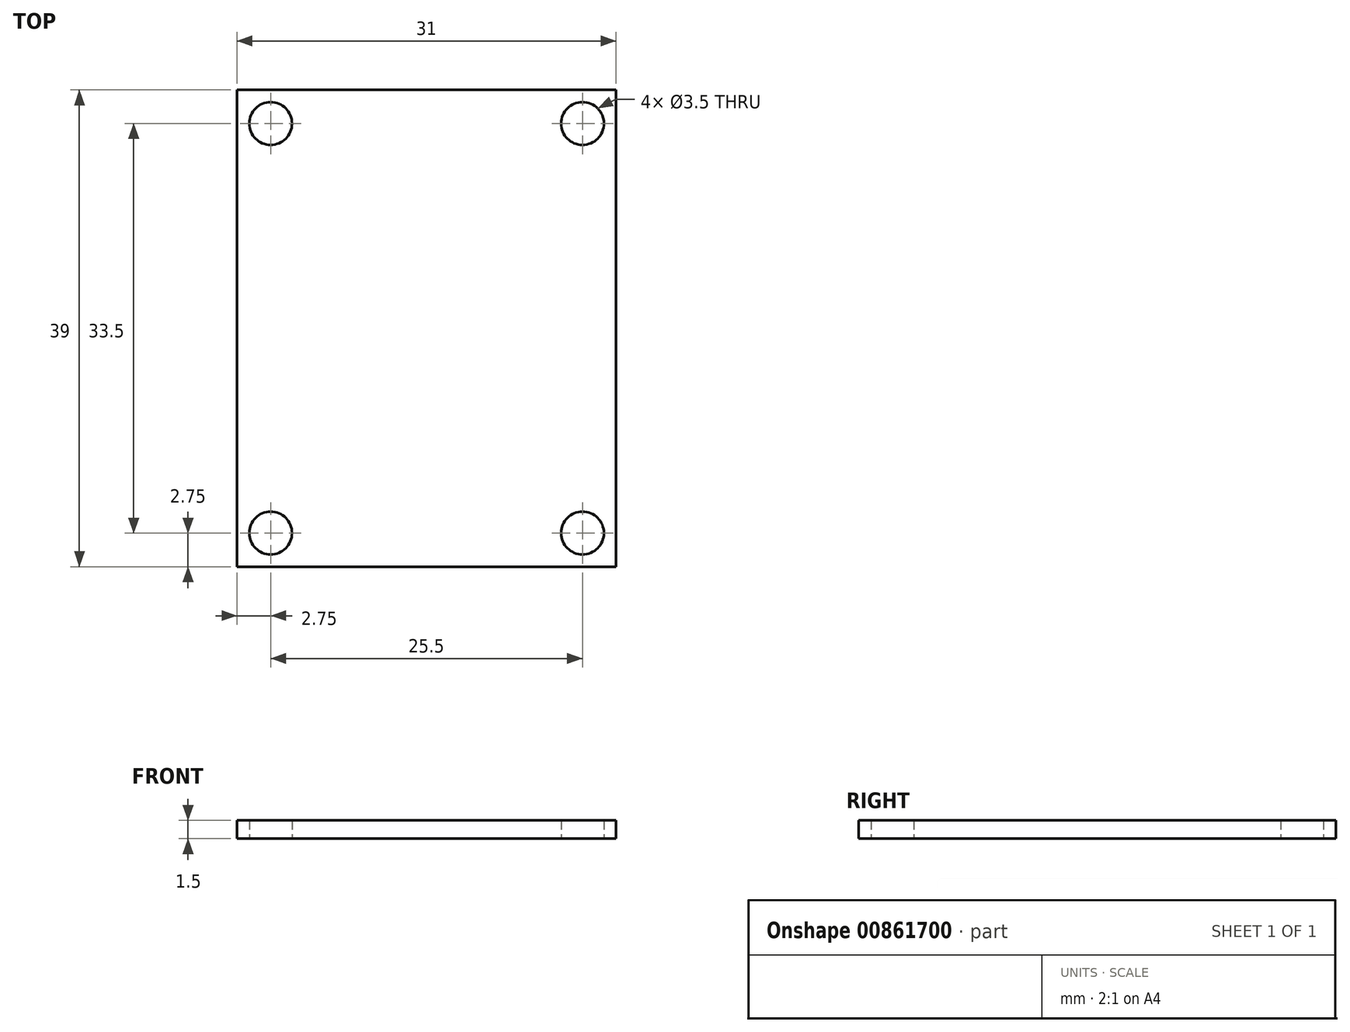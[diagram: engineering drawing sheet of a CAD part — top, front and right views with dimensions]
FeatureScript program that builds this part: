
annotation { "Feature Type Name" : "Feature", "Feature Type Description" : "" }
export const myFeature = defineFeature(function(context is Context, id is Id, definition is map)
    precondition{}
    {
        {
            var Q0;
            Q0=qCreatedBy(makeId("Top.planeOp"),FACE);
            var sketch = newSketch(context, id + "F0", { "sketchPlane" : qUnion([Q0])});
            skLineSegment(sketch, "E0.bottom", {"start": v(15.5, 19.5) * mm, "end": v(-15.5, 19.5) * mm});
            skLineSegment(sketch, "E0.top", {"start": v(15.5, -19.5) * mm, "end": v(-15.5, -19.5) * mm});
            skLineSegment(sketch, "E0.left", {"start": v(15.5, 19.5) * mm, "end": v(15.5, -19.5) * mm});
            skLineSegment(sketch, "E0.right", {"start": v(-15.5, 19.5) * mm, "end": v(-15.5, -19.5) * mm});
            skPoint(sketch, "E0.middle", {"position": v(0, 0) * mm});
            skCircle(sketch, "E1", {"center": v(-12.75, 16.75) * mm, "radius": 1.75 * mm});
            skCircle(sketch, "E2.MirrorC", {"center": v(-12.75, -16.75) * mm, "radius": 1.75 * mm});
            skCircle(sketch, "E3.MirrorC", {"center": v(12.75, 16.75) * mm, "radius": 1.75 * mm});
            skCircle(sketch, "E4.MirrorC", {"center": v(12.75, -16.75) * mm, "radius": 1.75 * mm});
            skSolve(sketch);
        }
        {
            var Q0;
            Q0=makeQuery(id+"F0.imprint","IMPRINT",FACE,{"disambiguationData":[TD([[makeQuery(id+"F0.imprint","IMPRINT",EDGE,{"derivedFrom":sQuery(id+"F0.wireOp",EDGE,"E0.bottom")}),1.0]])]});
            extrude(context, id + "F1", {"entities" : qUnion([Q0]), "depth" : 1.5 * mm, "offsetDistance" : 25 * mm});
        }
    });
